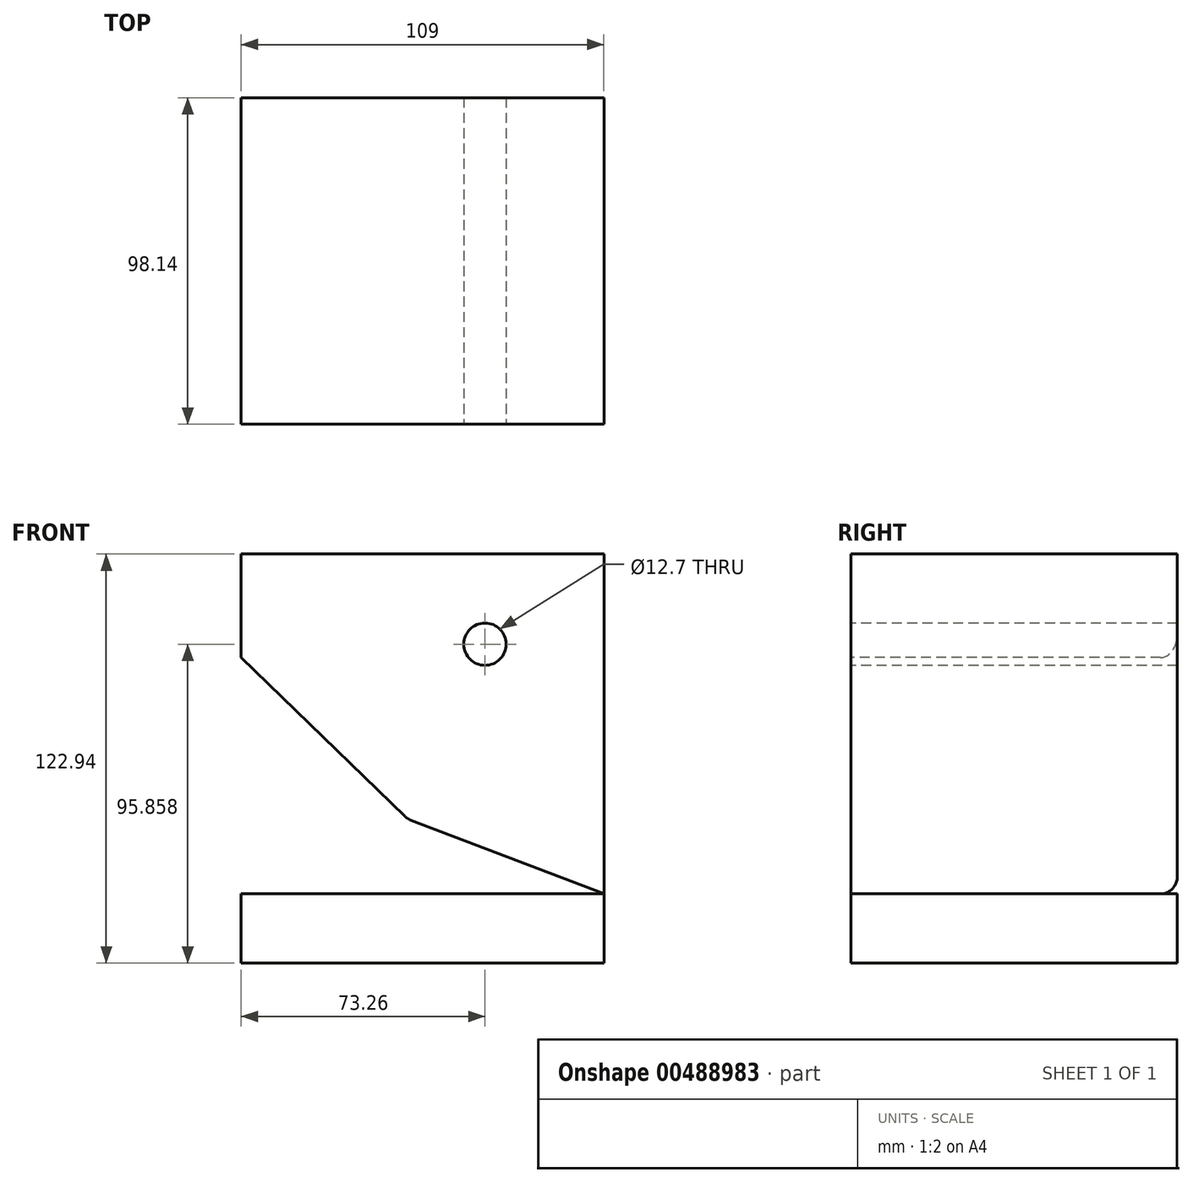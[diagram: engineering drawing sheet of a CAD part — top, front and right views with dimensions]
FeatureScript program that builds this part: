
annotation { "Feature Type Name" : "Feature", "Feature Type Description" : "" }
export const myFeature = defineFeature(function(context is Context, id is Id, definition is map)
    precondition{}
    {
        {
            var Q0;
            Q0=qCreatedBy(makeId("Top.planeOp"),FACE);
            var sketch = newSketch(context, id + "F0", { "sketchPlane" : qUnion([Q0])});
            skLineSegment(sketch, "E0.bottom", {"start": v(-54.5, 49.07) * mm, "end": v(54.5, 49.07) * mm});
            skLineSegment(sketch, "E0.top", {"start": v(-54.5, -49.07) * mm, "end": v(54.5, -49.07) * mm});
            skLineSegment(sketch, "E0.left", {"start": v(-54.5, 49.07) * mm, "end": v(-54.5, -49.07) * mm});
            skLineSegment(sketch, "E0.right", {"start": v(54.5, 49.07) * mm, "end": v(54.5, -49.07) * mm});
            skPoint(sketch, "E0.middle", {"position": v(0, 0) * mm});
            skSolve(sketch);
        }
        {
            var Q0;
            Q0=makeQuery(id+"F0.imprint","IMPRINT",FACE,{"disambiguationData":[TD([[makeQuery(id+"F0.imprint","IMPRINT",EDGE,{"derivedFrom":sQuery(id+"F0.wireOp",EDGE,"E0.bottom")}),-1.0]])]});
            extrude(context, id + "F1", {"entities" : qUnion([Q0]), "depth" : 122.94 * mm});
        }
        {
            var Q0;
            Q0=makeQuery(id+"F1.opExtrude","SWEPT_FACE",FACE,{"disambiguationData":[OSD([sQuery(id+"F0.wireOp",EDGE,"E0.top")])]});
            var sketch = newSketch(context, id + "F2", { "sketchPlane" : qUnion([Q0])});
            skLineSegment(sketch, "E1", {"start": v(-10.02, 122.94) * mm, "end": v(-54.5, 91.85) * mm});
            skLineSegment(sketch, "E2", {"start": v(-54.5, 91.85) * mm, "end": v(-4.55, 43.4) * mm});
            skLineSegment(sketch, "E3", {"start": v(-4.55, 43.4) * mm, "end": v(54.5, 20.82) * mm});
            skLineSegment(sketch, "E4", {"start": v(54.5, 20.82) * mm, "end": v(-54.5, 20.82) * mm});
            skLineSegment(sketch, "E5", {"start": v(-54.5, 20.82) * mm, "end": v(-54.5, 91.85) * mm});
            skSolve(sketch);
        }
        {
            var Q0;
            Q0=makeQuery(id+"F2.imprint","IMPRINT",FACE,{"disambiguationData":[TD([[makeQuery(id+"F2.imprint","IMPRINT",EDGE,{"derivedFrom":sQuery(id+"F2.wireOp",EDGE,"E2")}),-1.0]])]});
            extrude(context, id + "F3", {"entities" : qUnion([Q0]), "operationType" : NewBodyOperationType.REMOVE, "oppositeDirection" : true, "depth" : 228.6 * mm});
        }
        {
            var Q0;
            Q0=makeQuery(id+"F3.boolean.opBoolean","INTERSECT",EDGE,{"derivedFrom":[makeQuery(id+"F1.opExtrude","SWEPT_FACE",FACE,{"disambiguationData":[OSD([sQuery(id+"F0.wireOp",EDGE,"E0.bottom")])]}),makeQuery(id+"F3.opExtrude","SWEPT_FACE",FACE,{"disambiguationData":[OSD([sQuery(id+"F2.wireOp",EDGE,"E2")])]})]});
            var Q1;
            Q1=makeQuery(id+"F3.boolean.opBoolean","INTERSECT",EDGE,{"derivedFrom":[makeQuery(id+"F1.opExtrude","SWEPT_FACE",FACE,{"disambiguationData":[OSD([sQuery(id+"F0.wireOp",EDGE,"E0.bottom")])]}),makeQuery(id+"F3.opExtrude","SWEPT_FACE",FACE,{"disambiguationData":[OSD([sQuery(id+"F2.wireOp",EDGE,"E3")])]})]});
            var Q2;
            Q2=makeQuery(id+"F3.boolean.opBoolean","COPY",EDGE,{"derivedFrom":makeQuery(id+"F3.opExtrude","SWEPT_EDGE",EDGE,{"disambiguationData":[OSD([sQuery(id+"F2.wireOp",EDGE,"E2"),sQuery(id+"F2.wireOp",EDGE,"E3")])]})});
            var Q3;
            Q3=makeQuery(id+"F3.boolean.opBoolean","COPY",EDGE,{"derivedFrom":makeQuery(id+"F3.opExtrude","CAP_EDGE",EDGE,{"disambiguationData":[OSD([sQuery(id+"F2.wireOp",EDGE,"E2")])],"isStart":true})});
            var Q4;
            Q4=makeQuery(id+"F3.boolean.opBoolean","COPY",EDGE,{"derivedFrom":makeQuery(id+"F3.opExtrude","CAP_EDGE",EDGE,{"disambiguationData":[OSD([sQuery(id+"F2.wireOp",EDGE,"E3")])],"isStart":true})});
            fillet(context, id + "F4", {"entities" : qUnion([Q0, Q1, Q2, Q3, Q4]), "radius" : 5.08 * mm, "tangentPropagation" : true, "allowEdgeOverflow" : false});
        }
        {
            var Q0;
            {var subQ2=sQuery(id+"F0.wireOp",EDGE,"E0.top");Q0=makeQuery(id+"F3.boolean.opBoolean","SPLIT",FACE,{"disambiguationData":[TD([makeQuery(id+"F3.opExtrude","SWEPT_FACE",FACE,{"disambiguationData":[OSD([sQuery(id+"F2.wireOp",EDGE,"E2")])]})])],"derivedFrom":makeQuery(id+"F1.opExtrude","SWEPT_FACE",FACE,{"disambiguationData":[OSD([subQ2])]})});}
            var sketch = newSketch(context, id + "F5", { "sketchPlane" : qUnion([Q0])});
            skPoint(sketch, "E6", {"position": v(18.76, 95.86) * mm});
            skCircle(sketch, "E7", {"center": v(18.76, 95.86) * mm, "radius": 27.08 * mm});
            skSolve(sketch);
        }
        {
            var Q0;
            Q0=sQuery(id+"F5.wireOp",VERTEX,"E6");
            var Q1;
            Q1=makeQuery(id+"F3.boolean.opBoolean","SPLIT",BODY,{"disambiguationData":[OD(1.0)],"derivedFrom":makeQuery(id+"F1.opExtrude","SWEPT_BODY",BODY,{"disambiguationData":[OSD([sQuery(id+"F0.wireOp",EDGE,"E0.bottom"),sQuery(id+"F0.wireOp",EDGE,"E0.top"),sQuery(id+"F0.wireOp",EDGE,"E0.left"),sQuery(id+"F0.wireOp",EDGE,"E0.right")])]})});
            hole(context, id + "F6", {"style" : HoleStyle.SIMPLE, "endStyle" : HoleEndStyle.THROUGH, "holeDiameter" : 12.7 * mm, "isTappedThrough" : true, "tappedDepth" : 12.7 * mm, "tapClearance" : 3, "locations" : qUnion([Q0]), "scope" : qUnion([Q1])});
        }
    });
